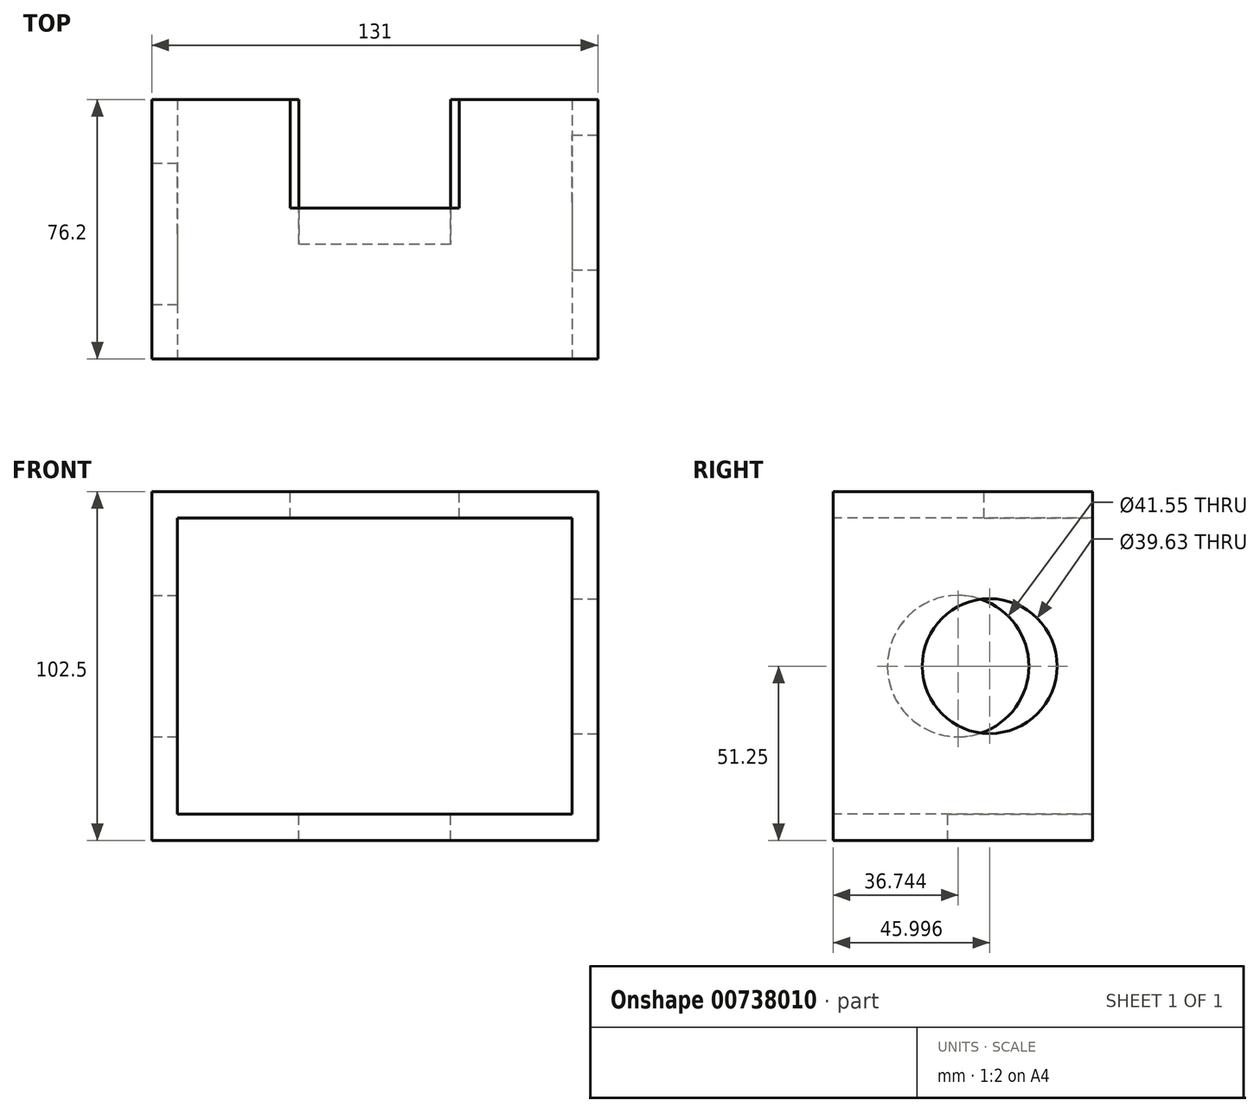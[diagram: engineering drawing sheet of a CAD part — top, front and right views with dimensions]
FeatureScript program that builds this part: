
annotation { "Feature Type Name" : "Feature", "Feature Type Description" : "" }
export const myFeature = defineFeature(function(context is Context, id is Id, definition is map)
    precondition{}
    {
        {
            var Q0;
            Q0=qCreatedBy(makeId("Front.planeOp"),FACE);
            var sketch = newSketch(context, id + "F0", { "sketchPlane" : qUnion([Q0])});
            skLineSegment(sketch, "E0.bottom", {"start": v(-65.5, 51.25) * mm, "end": v(65.5, 51.25) * mm});
            skLineSegment(sketch, "E0.top", {"start": v(-65.5, -51.25) * mm, "end": v(65.5, -51.25) * mm});
            skLineSegment(sketch, "E0.left", {"start": v(-65.5, 51.25) * mm, "end": v(-65.5, -51.25) * mm});
            skLineSegment(sketch, "E0.right", {"start": v(65.5, 51.25) * mm, "end": v(65.5, -51.25) * mm});
            skPoint(sketch, "E0.middle", {"position": v(0, 0) * mm});
            skSolve(sketch);
        }
        {
            var Q0;
            Q0 = qSketchRegion(id + "F0", true);
            extrude(context, id + "F1", {"entities" : qUnion([Q0]), "depth" : 76.2 * mm, "offsetDistance" : 25.4 * mm});
        }
        {
            var Q0;
            Q0=qCreatedBy(makeId("Front.planeOp"),FACE);
            var sketch = newSketch(context, id + "F2", { "sketchPlane" : qUnion([Q0])});
            skLineSegment(sketch, "E1.bottom", {"start": v(-57.95, 43.47) * mm, "end": v(57.95, 43.47) * mm});
            skLineSegment(sketch, "E1.top", {"start": v(-57.95, -43.47) * mm, "end": v(57.95, -43.47) * mm});
            skLineSegment(sketch, "E1.left", {"start": v(-57.95, 43.47) * mm, "end": v(-57.95, -43.47) * mm});
            skLineSegment(sketch, "E1.right", {"start": v(57.95, 43.47) * mm, "end": v(57.95, -43.47) * mm});
            skPoint(sketch, "E1.middle", {"position": v(0, 0) * mm});
            skSolve(sketch);
        }
        {
            var Q0;
            Q0 = qSketchRegion(id + "F2", true);
            extrude(context, id + "F3", {"entities" : qUnion([Q0]), "operationType" : NewBodyOperationType.REMOVE, "oppositeDirection" : true, "depth" : 76.2 * mm, "offsetDistance" : 25.4 * mm, "symmetric" : true});
        }
        {
            var Q0;
            Q0=makeQuery(id+"F3.boolean.opBoolean","COPY",FACE,{"derivedFrom":makeQuery(id+"F3.opExtrude","CAP_FACE",FACE,{"disambiguationData":[OSD([sQuery(id+"F2.wireOp",EDGE,"E1.bottom"),sQuery(id+"F2.wireOp",EDGE,"E1.top"),sQuery(id+"F2.wireOp",EDGE,"E1.left"),sQuery(id+"F2.wireOp",EDGE,"E1.right")])],"isStart":true})});
            extrude(context, id + "F4", {"entities" : qUnion([Q0]), "operationType" : NewBodyOperationType.REMOVE, "oppositeDirection" : true, "depth" : 25.4 * mm, "offsetDistance" : 25.4 * mm});
        }
        {
            var Q0;
            Q0=makeQuery(id+"F4.boolean.opBoolean","COPY",FACE,{"derivedFrom":makeQuery(id+"F4.opExtrude","CAP_FACE",FACE,{"disambiguationData":[OSD([sQuery(id+"F2.wireOp",EDGE,"E1.bottom"),sQuery(id+"F2.wireOp",EDGE,"E1.top"),sQuery(id+"F2.wireOp",EDGE,"E1.left"),sQuery(id+"F2.wireOp",EDGE,"E1.right")])],"isStart":false})});
            extrude(context, id + "F5", {"entities" : qUnion([Q0]), "operationType" : NewBodyOperationType.REMOVE, "oppositeDirection" : true, "depth" : 76.2 * mm, "offsetDistance" : 25.4 * mm});
        }
        {
            var Q0;
            Q0=qCreatedBy(makeId("Top.planeOp"),FACE);
            var sketch = newSketch(context, id + "F6", { "sketchPlane" : qUnion([Q0])});
            skLineSegment(sketch, "E2.bottom", {"start": v(22.31, 0) * mm, "end": v(-22.31, 0) * mm});
            skLineSegment(sketch, "E2.top", {"start": v(22.31, -42.55) * mm, "end": v(-22.31, -42.55) * mm});
            skLineSegment(sketch, "E2.left", {"start": v(22.31, 0) * mm, "end": v(22.31, -42.55) * mm});
            skLineSegment(sketch, "E2.right", {"start": v(-22.31, 0) * mm, "end": v(-22.31, -42.55) * mm});
            skPoint(sketch, "E2.middle", {"position": v(0, -21.28) * mm});
            skSolve(sketch);
        }
        {
            var Q0;
            Q0 = qSketchRegion(id + "F6", true);
            extrude(context, id + "F7", {"entities" : qUnion([Q0]), "operationType" : NewBodyOperationType.REMOVE, "oppositeDirection" : true, "depth" : 76.2 * mm, "offsetDistance" : 25.4 * mm});
        }
        {
            var Q0;
            Q0=makeQuery(id+"F1.opExtrude","SWEPT_FACE",FACE,{"disambiguationData":[OSD([sQuery(id+"F0.wireOp",EDGE,"E0.bottom")])]});
            var sketch = newSketch(context, id + "F8", { "sketchPlane" : qUnion([Q0])});
            skLineSegment(sketch, "E3.bottom", {"start": v(-24.84, 0) * mm, "end": v(24.84, 0) * mm});
            skLineSegment(sketch, "E3.top", {"start": v(-24.84, -31.86) * mm, "end": v(24.84, -31.86) * mm});
            skLineSegment(sketch, "E3.left", {"start": v(-24.84, 0) * mm, "end": v(-24.84, -31.86) * mm});
            skLineSegment(sketch, "E3.right", {"start": v(24.84, 0) * mm, "end": v(24.84, -31.86) * mm});
            skPoint(sketch, "E3.middle", {"position": v(0, -15.93) * mm});
            skSolve(sketch);
        }
        {
            var Q0;
            Q0=makeQuery(id+"F8.imprint","IMPRINT",FACE,{"disambiguationData":[TD([[makeQuery(id+"F8.imprint","IMPRINT",EDGE,{"derivedFrom":sQuery(id+"F8.wireOp",EDGE,"E3.bottom")}),-1.0]])]});
            extrude(context, id + "F9", {"entities" : qUnion([Q0]), "operationType" : NewBodyOperationType.REMOVE, "oppositeDirection" : true, "depth" : 76.2 * mm, "offsetDistance" : 25.4 * mm});
        }
        {
            var Q0;
            Q0=qCreatedBy(makeId("Right.planeOp"),FACE);
            var sketch = newSketch(context, id + "F10", { "sketchPlane" : qUnion([Q0])});
            skCircle(sketch, "E4", {"center": v(-39.46, 0) * mm, "radius": 20.77 * mm});
            skSolve(sketch);
        }
        {
            var Q0;
            Q0 = qSketchRegion(id + "F10", true);
            extrude(context, id + "F11", {"entities" : qUnion([Q0]), "operationType" : NewBodyOperationType.REMOVE, "oppositeDirection" : true, "depth" : 76.2 * mm, "offsetDistance" : 25.4 * mm});
        }
        {
            var Q0;
            Q0=makeQuery(id+"F1.opExtrude","SWEPT_FACE",FACE,{"disambiguationData":[OSD([sQuery(id+"F0.wireOp",EDGE,"E0.right")])]});
            var sketch = newSketch(context, id + "F12", { "sketchPlane" : qUnion([Q0])});
            skCircle(sketch, "E5", {"center": v(-30.2, 0) * mm, "radius": 19.81 * mm});
            skSolve(sketch);
        }
        {
            var Q0;
            Q0 = qSketchRegion(id + "F12", true);
            extrude(context, id + "F13", {"entities" : qUnion([Q0]), "operationType" : NewBodyOperationType.REMOVE, "oppositeDirection" : true, "depth" : 25.4 * mm, "offsetDistance" : 25.4 * mm});
        }
    });
